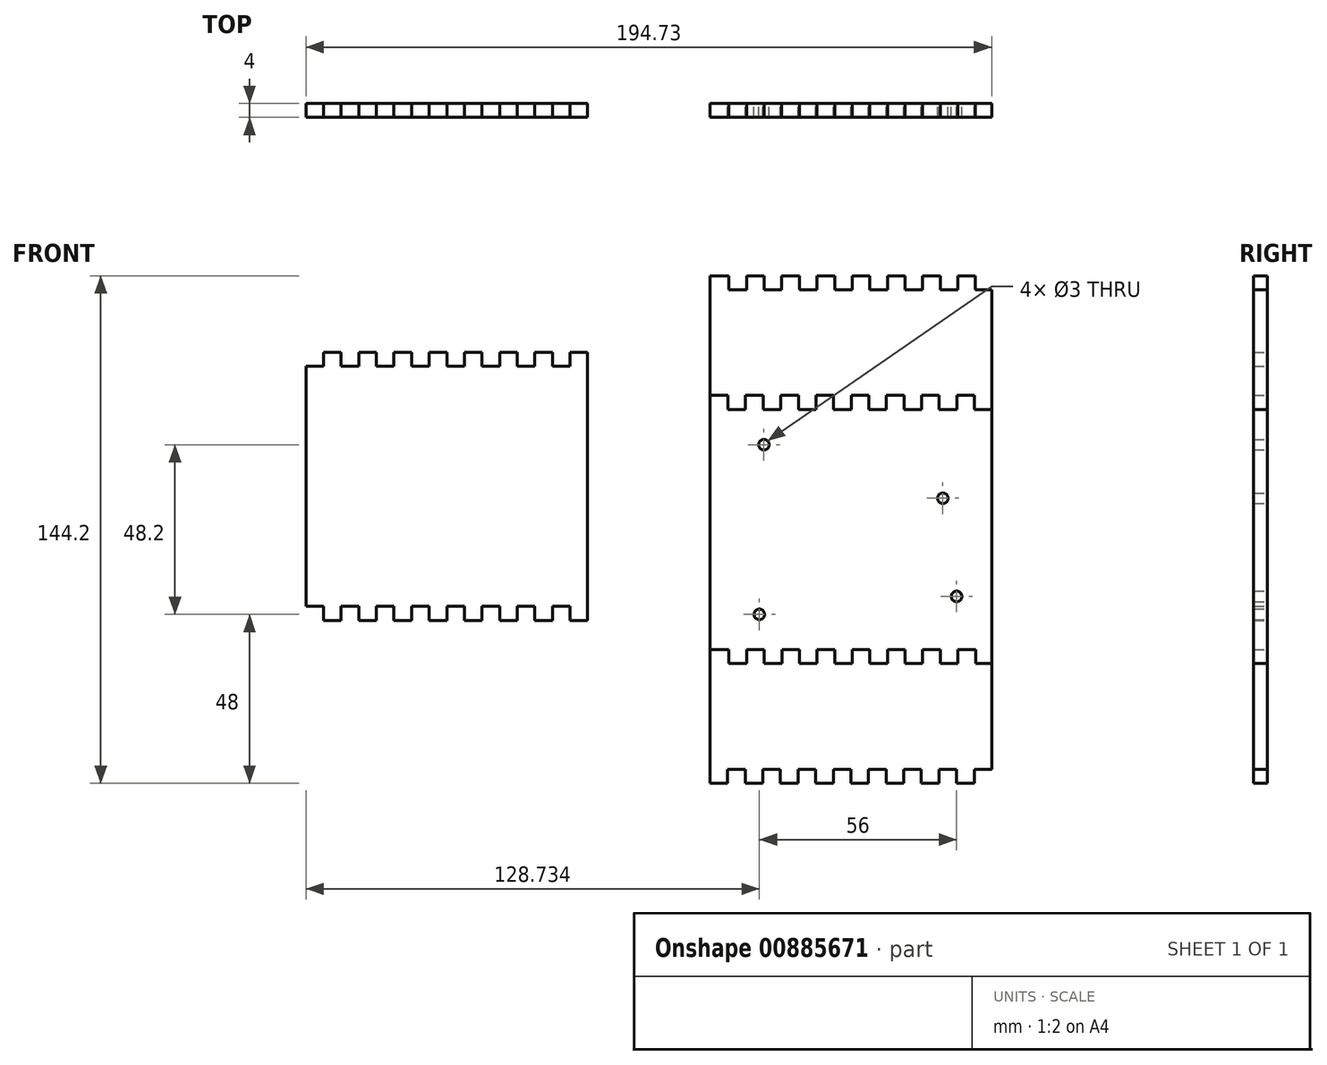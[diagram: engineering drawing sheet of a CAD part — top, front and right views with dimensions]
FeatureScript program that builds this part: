
annotation { "Feature Type Name" : "Feature", "Feature Type Description" : "" }
export const myFeature = defineFeature(function(context is Context, id is Id, definition is map)
    precondition{}
    {
        {
            var Q0;
            Q0=qCreatedBy(makeId("Front.planeOp"),FACE);
            var sketch = newSketch(context, id + "F0", { "sketchPlane" : qUnion([Q0])});
            skLineSegment(sketch, "E0.top", {"start": v(-30.4, -49.1) * mm, "end": v(-25.4, -49.1) * mm});
            skLineSegment(sketch, "E0.left", {"start": v(-35.8, 27.1) * mm, "end": v(-35.8, -45.1) * mm});
            skLineSegment(sketch, "E0.right", {"start": v(44.2, 23.1) * mm, "end": v(44.2, -49.1) * mm});
            skLineSegment(sketch, "E1.1.0.0", {"start": v(-30.7, 23.1) * mm, "end": v(-25.7, 23.1) * mm});
            skLineSegment(sketch, "E1.1.0.1", {"start": v(-30.7, 27.1) * mm, "end": v(-30.7, 23.1) * mm});
            skLineSegment(sketch, "E1.1.0.2", {"start": v(-25.7, 27.1) * mm, "end": v(-25.7, 23.1) * mm});
            skLineSegment(sketch, "E1.2.0.0", {"start": v(-20.7, 23.1) * mm, "end": v(-15.7, 23.1) * mm});
            skLineSegment(sketch, "E1.2.0.1", {"start": v(-20.7, 27.1) * mm, "end": v(-20.7, 23.1) * mm});
            skLineSegment(sketch, "E1.2.0.2", {"start": v(-15.7, 27.1) * mm, "end": v(-15.7, 23.1) * mm});
            skLineSegment(sketch, "E1.3.0.0", {"start": v(-10.7, 23.1) * mm, "end": v(-5.7, 23.1) * mm});
            skLineSegment(sketch, "E1.3.0.1", {"start": v(-10.7, 27.1) * mm, "end": v(-10.7, 23.1) * mm});
            skLineSegment(sketch, "E1.3.0.2", {"start": v(-5.7, 27.1) * mm, "end": v(-5.7, 23.1) * mm});
            skLineSegment(sketch, "E1.4.0.0", {"start": v(-0.7, 23.1) * mm, "end": v(4.3, 23.1) * mm});
            skLineSegment(sketch, "E1.4.0.1", {"start": v(-0.7, 27.1) * mm, "end": v(-0.7, 23.1) * mm});
            skLineSegment(sketch, "E1.4.0.2", {"start": v(4.3, 27.1) * mm, "end": v(4.3, 23.1) * mm});
            skLineSegment(sketch, "E1.5.0.0", {"start": v(9.3, 23.1) * mm, "end": v(14.3, 23.1) * mm});
            skLineSegment(sketch, "E1.5.0.1", {"start": v(9.3, 27.1) * mm, "end": v(9.3, 23.1) * mm});
            skLineSegment(sketch, "E1.5.0.2", {"start": v(14.3, 27.1) * mm, "end": v(14.3, 23.1) * mm});
            skLineSegment(sketch, "E1.6.0.0", {"start": v(19.3, 23.1) * mm, "end": v(24.3, 23.1) * mm});
            skLineSegment(sketch, "E1.6.0.1", {"start": v(19.3, 27.1) * mm, "end": v(19.3, 23.1) * mm});
            skLineSegment(sketch, "E1.6.0.2", {"start": v(24.3, 27.1) * mm, "end": v(24.3, 23.1) * mm});
            skLineSegment(sketch, "E1.7.0.0", {"start": v(29.3, 23.1) * mm, "end": v(34.3, 23.1) * mm});
            skLineSegment(sketch, "E1.7.0.1", {"start": v(29.3, 27.1) * mm, "end": v(29.3, 23.1) * mm});
            skLineSegment(sketch, "E1.7.0.2", {"start": v(34.3, 27.1) * mm, "end": v(34.3, 23.1) * mm});
            skLineSegment(sketch, "E1.8.0.0", {"start": v(39.3, 23.1) * mm, "end": v(44.2, 23.1) * mm});
            skLineSegment(sketch, "E1.8.0.1", {"start": v(39.3, 27.1) * mm, "end": v(39.3, 23.1) * mm});
            skLineSegment(sketch, "E2.trimOffspring", {"start": v(-25.7, 27.1) * mm, "end": v(-20.7, 27.1) * mm});
            skLineSegment(sketch, "E3.trimOffspring", {"start": v(-15.7, 27.1) * mm, "end": v(-10.7, 27.1) * mm});
            skLineSegment(sketch, "E4.trimOffspring", {"start": v(-5.7, 27.1) * mm, "end": v(-0.7, 27.1) * mm});
            skLineSegment(sketch, "E5.trimOffspring", {"start": v(4.3, 27.1) * mm, "end": v(9.3, 27.1) * mm});
            skLineSegment(sketch, "E6.trimOffspring", {"start": v(14.3, 27.1) * mm, "end": v(19.3, 27.1) * mm});
            skLineSegment(sketch, "E7.trimOffspring", {"start": v(24.3, 27.1) * mm, "end": v(29.3, 27.1) * mm});
            skLineSegment(sketch, "E8.trimOffspring", {"start": v(34.3, 27.1) * mm, "end": v(39.3, 27.1) * mm});
            skLineSegment(sketch, "E9", {"start": v(44.2, 23.1) * mm, "end": v(44.2, 57.1) * mm});
            skLineSegment(sketch, "E10", {"start": v(39.57, 61.1) * mm, "end": v(34.57, 61.1) * mm});
            skLineSegment(sketch, "E11", {"start": v(-35.8, 61.1) * mm, "end": v(-35.8, 27.1) * mm});
            skCircle(sketch, "E12", {"center": v(30.3, -2.1) * mm, "radius": 1.5 * mm});
            skCircle(sketch, "E13", {"center": v(34.2, -30) * mm, "radius": 1.5 * mm});
            skCircle(sketch, "E14", {"center": v(-20.5, 13.1) * mm, "radius": 1.5 * mm});
            skCircle(sketch, "E15", {"center": v(-21.8, -35.1) * mm, "radius": 1.5 * mm});
            skLineSegment(sketch, "E16", {"start": v(-30.7, 27.1) * mm, "end": v(-35.8, 27.1) * mm});
            skLineSegment(sketch, "E17.1.0.1", {"start": v(-30.4, -45.1) * mm, "end": v(-30.4, -49.1) * mm});
            skLineSegment(sketch, "E17.1.0.2", {"start": v(-25.4, -45.1) * mm, "end": v(-25.4, -49.1) * mm});
            skLineSegment(sketch, "E17.2.0.0", {"start": v(-20.4, -49.1) * mm, "end": v(-15.4, -49.1) * mm});
            skLineSegment(sketch, "E17.2.0.1", {"start": v(-20.4, -45.1) * mm, "end": v(-20.4, -49.1) * mm});
            skLineSegment(sketch, "E17.2.0.2", {"start": v(-15.4, -45.1) * mm, "end": v(-15.4, -49.1) * mm});
            skLineSegment(sketch, "E17.3.0.0", {"start": v(-10.4, -49.1) * mm, "end": v(-5.4, -49.1) * mm});
            skLineSegment(sketch, "E17.3.0.1", {"start": v(-10.4, -45.1) * mm, "end": v(-10.4, -49.1) * mm});
            skLineSegment(sketch, "E17.3.0.2", {"start": v(-5.4, -45.1) * mm, "end": v(-5.4, -49.1) * mm});
            skLineSegment(sketch, "E17.4.0.0", {"start": v(-0.4, -49.1) * mm, "end": v(4.6, -49.1) * mm});
            skLineSegment(sketch, "E17.4.0.1", {"start": v(-0.4, -45.1) * mm, "end": v(-0.4, -49.1) * mm});
            skLineSegment(sketch, "E17.4.0.2", {"start": v(4.6, -45.1) * mm, "end": v(4.6, -49.1) * mm});
            skLineSegment(sketch, "E17.5.0.0", {"start": v(9.6, -49.1) * mm, "end": v(14.6, -49.1) * mm});
            skLineSegment(sketch, "E17.5.0.1", {"start": v(9.6, -45.1) * mm, "end": v(9.6, -49.1) * mm});
            skLineSegment(sketch, "E17.5.0.2", {"start": v(14.6, -45.1) * mm, "end": v(14.6, -49.1) * mm});
            skLineSegment(sketch, "E17.6.0.0", {"start": v(19.6, -49.1) * mm, "end": v(24.6, -49.1) * mm});
            skLineSegment(sketch, "E17.6.0.1", {"start": v(19.6, -45.1) * mm, "end": v(19.6, -49.1) * mm});
            skLineSegment(sketch, "E17.6.0.2", {"start": v(24.6, -45.1) * mm, "end": v(24.6, -49.1) * mm});
            skLineSegment(sketch, "E17.7.0.0", {"start": v(29.6, -49.1) * mm, "end": v(34.6, -49.1) * mm});
            skLineSegment(sketch, "E17.7.0.1", {"start": v(29.6, -45.1) * mm, "end": v(29.6, -49.1) * mm});
            skLineSegment(sketch, "E17.7.0.2", {"start": v(34.6, -45.1) * mm, "end": v(34.6, -49.1) * mm});
            skLineSegment(sketch, "E17.8.0.1", {"start": v(39.6, -45.1) * mm, "end": v(39.6, -49.1) * mm});
            skLineSegment(sketch, "E18.trimOffspring", {"start": v(-25.4, -45.1) * mm, "end": v(-20.4, -45.1) * mm});
            skLineSegment(sketch, "E19.trimOffspring", {"start": v(-15.4, -45.1) * mm, "end": v(-10.4, -45.1) * mm});
            skLineSegment(sketch, "E20.trimOffspring", {"start": v(-5.4, -45.1) * mm, "end": v(-0.4, -45.1) * mm});
            skLineSegment(sketch, "E21.trimOffspring", {"start": v(4.6, -45.1) * mm, "end": v(9.6, -45.1) * mm});
            skLineSegment(sketch, "E22.trimOffspring", {"start": v(14.6, -45.1) * mm, "end": v(19.6, -45.1) * mm});
            skLineSegment(sketch, "E23.trimOffspring", {"start": v(24.6, -45.1) * mm, "end": v(29.6, -45.1) * mm});
            skLineSegment(sketch, "E24.trimOffspring", {"start": v(34.6, -45.1) * mm, "end": v(39.6, -45.1) * mm});
            skLineSegment(sketch, "E25", {"start": v(-30.4, -45.1) * mm, "end": v(-35.8, -45.1) * mm});
            skLineSegment(sketch, "E26.trimOffspring", {"start": v(39.6, -49.1) * mm, "end": v(44.2, -49.1) * mm});
            skLineSegment(sketch, "E27.top", {"start": v(-30.43, 57.1) * mm, "end": v(-25.43, 57.1) * mm});
            skLineSegment(sketch, "E27.left", {"start": v(-30.43, 61.1) * mm, "end": v(-30.43, 57.1) * mm});
            skLineSegment(sketch, "E27.right", {"start": v(-25.43, 61.1) * mm, "end": v(-25.43, 57.1) * mm});
            skLineSegment(sketch, "E28.trimOffspring", {"start": v(-30.43, 61.1) * mm, "end": v(-35.8, 61.1) * mm});
            skLineSegment(sketch, "E29.1.0.0", {"start": v(-20.43, 61.1) * mm, "end": v(-20.43, 57.1) * mm});
            skLineSegment(sketch, "E29.1.0.1", {"start": v(-20.43, 57.1) * mm, "end": v(-15.43, 57.1) * mm});
            skLineSegment(sketch, "E29.1.0.2", {"start": v(-15.43, 61.1) * mm, "end": v(-15.43, 57.1) * mm});
            skLineSegment(sketch, "E29.2.0.0", {"start": v(-10.43, 61.1) * mm, "end": v(-10.43, 57.1) * mm});
            skLineSegment(sketch, "E29.2.0.1", {"start": v(-10.43, 57.1) * mm, "end": v(-5.43, 57.1) * mm});
            skLineSegment(sketch, "E29.2.0.2", {"start": v(-5.43, 61.1) * mm, "end": v(-5.43, 57.1) * mm});
            skLineSegment(sketch, "E29.3.0.0", {"start": v(-0.43, 61.1) * mm, "end": v(-0.43, 57.1) * mm});
            skLineSegment(sketch, "E29.3.0.1", {"start": v(-0.43, 57.1) * mm, "end": v(4.57, 57.1) * mm});
            skLineSegment(sketch, "E29.3.0.2", {"start": v(4.57, 61.1) * mm, "end": v(4.57, 57.1) * mm});
            skLineSegment(sketch, "E29.4.0.0", {"start": v(9.57, 61.1) * mm, "end": v(9.57, 57.1) * mm});
            skLineSegment(sketch, "E29.4.0.1", {"start": v(9.57, 57.1) * mm, "end": v(14.57, 57.1) * mm});
            skLineSegment(sketch, "E29.4.0.2", {"start": v(14.57, 61.1) * mm, "end": v(14.57, 57.1) * mm});
            skLineSegment(sketch, "E29.5.0.0", {"start": v(19.57, 61.1) * mm, "end": v(19.57, 57.1) * mm});
            skLineSegment(sketch, "E29.5.0.1", {"start": v(19.57, 57.1) * mm, "end": v(24.57, 57.1) * mm});
            skLineSegment(sketch, "E29.5.0.2", {"start": v(24.57, 61.1) * mm, "end": v(24.57, 57.1) * mm});
            skLineSegment(sketch, "E29.6.0.0", {"start": v(29.57, 61.1) * mm, "end": v(29.57, 57.1) * mm});
            skLineSegment(sketch, "E29.6.0.1", {"start": v(29.57, 57.1) * mm, "end": v(34.57, 57.1) * mm});
            skLineSegment(sketch, "E29.6.0.2", {"start": v(34.57, 61.1) * mm, "end": v(34.57, 57.1) * mm});
            skLineSegment(sketch, "E29.7.0.0", {"start": v(39.57, 61.1) * mm, "end": v(39.57, 57.1) * mm});
            skLineSegment(sketch, "E29.direction1", {"start": v(-30.43, 57.1) * mm, "end": v(-20.43, 57.1) * mm, "construction": true});
            skLineSegment(sketch, "E30", {"start": v(39.57, 57.1) * mm, "end": v(44.2, 57.1) * mm});
            skLineSegment(sketch, "E31.trimOffspring", {"start": v(-20.43, 61.1) * mm, "end": v(-25.43, 61.1) * mm});
            skLineSegment(sketch, "E32.trimOffspring", {"start": v(-10.43, 61.1) * mm, "end": v(-15.43, 61.1) * mm});
            skLineSegment(sketch, "E33.trimOffspring", {"start": v(-0.43, 61.1) * mm, "end": v(-5.43, 61.1) * mm});
            skLineSegment(sketch, "E34.trimOffspring", {"start": v(9.57, 61.1) * mm, "end": v(4.57, 61.1) * mm});
            skLineSegment(sketch, "E35.trimOffspring", {"start": v(19.57, 61.1) * mm, "end": v(14.57, 61.1) * mm});
            skLineSegment(sketch, "E36.trimOffspring", {"start": v(29.57, 61.1) * mm, "end": v(24.57, 61.1) * mm});
            skLineSegment(sketch, "E37.top", {"start": v(-30.8, -79.1) * mm, "end": v(-25.8, -79.1) * mm});
            skLineSegment(sketch, "E37.left", {"start": v(-30.8, -83.1) * mm, "end": v(-30.8, -79.1) * mm});
            skLineSegment(sketch, "E37.right", {"start": v(-25.8, -83.1) * mm, "end": v(-25.8, -79.1) * mm});
            skLineSegment(sketch, "E38.1.0.0", {"start": v(-20.8, -83.1) * mm, "end": v(-20.8, -79.1) * mm});
            skLineSegment(sketch, "E38.1.0.1", {"start": v(-20.8, -79.1) * mm, "end": v(-15.8, -79.1) * mm});
            skLineSegment(sketch, "E38.1.0.2", {"start": v(-15.8, -83.1) * mm, "end": v(-15.8, -79.1) * mm});
            skLineSegment(sketch, "E38.2.0.0", {"start": v(-10.8, -83.1) * mm, "end": v(-10.8, -79.1) * mm});
            skLineSegment(sketch, "E38.2.0.1", {"start": v(-10.8, -79.1) * mm, "end": v(-5.8, -79.1) * mm});
            skLineSegment(sketch, "E38.2.0.2", {"start": v(-5.8, -83.1) * mm, "end": v(-5.8, -79.1) * mm});
            skLineSegment(sketch, "E38.3.0.0", {"start": v(-0.8, -83.1) * mm, "end": v(-0.8, -79.1) * mm});
            skLineSegment(sketch, "E38.3.0.1", {"start": v(-0.8, -79.1) * mm, "end": v(4.2, -79.1) * mm});
            skLineSegment(sketch, "E38.3.0.2", {"start": v(4.2, -83.1) * mm, "end": v(4.2, -79.1) * mm});
            skLineSegment(sketch, "E38.4.0.0", {"start": v(9.2, -83.1) * mm, "end": v(9.2, -79.1) * mm});
            skLineSegment(sketch, "E38.4.0.1", {"start": v(9.2, -79.1) * mm, "end": v(14.2, -79.1) * mm});
            skLineSegment(sketch, "E38.4.0.2", {"start": v(14.2, -83.1) * mm, "end": v(14.2, -79.1) * mm});
            skLineSegment(sketch, "E38.5.0.0", {"start": v(19.2, -83.1) * mm, "end": v(19.2, -79.1) * mm});
            skLineSegment(sketch, "E38.5.0.1", {"start": v(19.2, -79.1) * mm, "end": v(24.2, -79.1) * mm});
            skLineSegment(sketch, "E38.5.0.2", {"start": v(24.2, -83.1) * mm, "end": v(24.2, -79.1) * mm});
            skLineSegment(sketch, "E38.6.0.0", {"start": v(29.2, -83.1) * mm, "end": v(29.2, -79.1) * mm});
            skLineSegment(sketch, "E38.6.0.1", {"start": v(29.2, -79.1) * mm, "end": v(34.2, -79.1) * mm});
            skLineSegment(sketch, "E38.6.0.2", {"start": v(34.2, -83.1) * mm, "end": v(34.2, -79.1) * mm});
            skLineSegment(sketch, "E38.7.0.0", {"start": v(39.2, -83.1) * mm, "end": v(39.2, -79.1) * mm});
            skLineSegment(sketch, "E38.direction1", {"start": v(-25.8, -83.1) * mm, "end": v(-20.8, -83.1) * mm, "construction": true});
            skLineSegment(sketch, "E39.trimOffspring", {"start": v(-20.8, -83.1) * mm, "end": v(-25.8, -83.1) * mm});
            skLineSegment(sketch, "E40.trimOffspring", {"start": v(-10.8, -83.1) * mm, "end": v(-15.8, -83.1) * mm});
            skLineSegment(sketch, "E41.trimOffspring", {"start": v(-0.8, -83.1) * mm, "end": v(-5.8, -83.1) * mm});
            skLineSegment(sketch, "E42.trimOffspring", {"start": v(9.2, -83.1) * mm, "end": v(4.2, -83.1) * mm});
            skLineSegment(sketch, "E43.trimOffspring", {"start": v(19.2, -83.1) * mm, "end": v(14.2, -83.1) * mm});
            skLineSegment(sketch, "E44.trimOffspring", {"start": v(29.2, -83.1) * mm, "end": v(24.2, -83.1) * mm});
            skLineSegment(sketch, "E45.trimOffspring", {"start": v(-30.8, -83.1) * mm, "end": v(-35.8, -83.1) * mm});
            skLineSegment(sketch, "E46", {"start": v(34.2, -83.1) * mm, "end": v(39.2, -83.1) * mm});
            skLineSegment(sketch, "E47", {"start": v(39.2, -79.1) * mm, "end": v(44.2, -79.1) * mm});
            skLineSegment(sketch, "E48", {"start": v(44.2, -79.1) * mm, "end": v(44.2, -49.1) * mm});
            skLineSegment(sketch, "E49", {"start": v(-35.8, -45.1) * mm, "end": v(-35.8, -83.1) * mm});
            skLineSegment(sketch, "E50.MirrorCS", {"start": v(-145.54, 39.34) * mm, "end": v(-140.54, 39.34) * mm});
            skLineSegment(sketch, "E51.MirrorCS", {"start": v(-140.54, 35.34) * mm, "end": v(-140.54, 39.34) * mm});
            skLineSegment(sketch, "E52.MirrorCS", {"start": v(-115.54, 35.34) * mm, "end": v(-120.54, 35.34) * mm});
            skLineSegment(sketch, "E53.MirrorCS", {"start": v(-135.54, 35.34) * mm, "end": v(-140.54, 35.34) * mm});
            skLineSegment(sketch, "E54.MirrorCS", {"start": v(-85.54, 35.34) * mm, "end": v(-90.54, 35.34) * mm});
            skLineSegment(sketch, "E55.MirrorCS", {"start": v(-135.54, 35.34) * mm, "end": v(-135.54, 39.34) * mm});
            skLineSegment(sketch, "E56.MirrorCS", {"start": v(-135.54, 39.34) * mm, "end": v(-130.54, 39.34) * mm});
            skLineSegment(sketch, "E57.MirrorCS", {"start": v(-80.54, 35.34) * mm, "end": v(-80.54, 39.34) * mm});
            skLineSegment(sketch, "E58.MirrorCS", {"start": v(-75.54, 35.34) * mm, "end": v(-80.54, 35.34) * mm});
            skLineSegment(sketch, "E59.MirrorCS", {"start": v(-120.54, 35.34) * mm, "end": v(-120.54, 39.34) * mm});
            skLineSegment(sketch, "E60.MirrorCS", {"start": v(-90.54, 35.34) * mm, "end": v(-90.54, 39.34) * mm});
            skLineSegment(sketch, "E61.MirrorCS", {"start": v(-85.54, 35.34) * mm, "end": v(-85.54, 39.34) * mm});
            skLineSegment(sketch, "E62.MirrorCS", {"start": v(-100.54, 35.34) * mm, "end": v(-100.54, 39.34) * mm});
            skLineSegment(sketch, "E63.MirrorCS", {"start": v(-105.54, 35.34) * mm, "end": v(-105.54, 39.34) * mm});
            skLineSegment(sketch, "E64.MirrorCS", {"start": v(-95.54, 35.34) * mm, "end": v(-95.54, 39.34) * mm});
            skLineSegment(sketch, "E65.MirrorCS", {"start": v(-105.54, 35.34) * mm, "end": v(-110.54, 35.34) * mm});
            skLineSegment(sketch, "E66.MirrorCS", {"start": v(-145.54, 35.34) * mm, "end": v(-145.54, 39.34) * mm});
            skLineSegment(sketch, "E67.MirrorCS", {"start": v(-95.54, 35.34) * mm, "end": v(-100.54, 35.34) * mm});
            skLineSegment(sketch, "E68.MirrorCS", {"start": v(-85.54, 39.34) * mm, "end": v(-80.54, 39.34) * mm});
            skLineSegment(sketch, "E69.MirrorCS", {"start": v(-110.54, 35.34) * mm, "end": v(-110.54, 39.34) * mm});
            skLineSegment(sketch, "E70.MirrorCS", {"start": v(-75.54, 35.34) * mm, "end": v(-75.54, 39.34) * mm});
            skLineSegment(sketch, "E71.MirrorCS", {"start": v(-125.54, 35.34) * mm, "end": v(-130.54, 35.34) * mm});
            skLineSegment(sketch, "E72.MirrorCS", {"start": v(-145.54, 35.34) * mm, "end": v(-150.54, 35.34) * mm});
            skLineSegment(sketch, "E73.MirrorCS", {"start": v(-125.54, 35.34) * mm, "end": v(-125.54, 39.34) * mm});
            skLineSegment(sketch, "E74.MirrorCS", {"start": v(-115.54, 35.34) * mm, "end": v(-115.54, 39.34) * mm});
            skLineSegment(sketch, "E75.MirrorCS", {"start": v(-95.54, 39.34) * mm, "end": v(-90.54, 39.34) * mm});
            skLineSegment(sketch, "E76.MirrorCS", {"start": v(-115.54, 39.34) * mm, "end": v(-110.54, 39.34) * mm});
            skLineSegment(sketch, "E77.MirrorCS", {"start": v(-105.54, 39.34) * mm, "end": v(-100.54, 39.34) * mm});
            skLineSegment(sketch, "E78.MirrorCS", {"start": v(-125.54, 39.34) * mm, "end": v(-120.54, 39.34) * mm});
            skLineSegment(sketch, "E79.MirrorCS", {"start": v(-130.54, 35.34) * mm, "end": v(-130.54, 39.34) * mm});
            skLineSegment(sketch, "E80.MirrorCS", {"start": v(-75.54, 39.34) * mm, "end": v(-70.54, 39.34) * mm});
            skLineSegment(sketch, "E81.MirrorCS", {"start": v(-150.54, -32.86) * mm, "end": v(-150.54, 35.34) * mm});
            skLineSegment(sketch, "E82.MirrorCS", {"start": v(-70.54, 39.34) * mm, "end": v(-70.54, -36.86) * mm});
            skLineSegment(sketch, "E83.MirrorCS", {"start": v(-80.54, -32.86) * mm, "end": v(-80.54, -36.86) * mm});
            skLineSegment(sketch, "E84.MirrorCS", {"start": v(-105.54, -32.86) * mm, "end": v(-105.54, -36.86) * mm});
            skLineSegment(sketch, "E85.MirrorCS", {"start": v(-85.54, -32.86) * mm, "end": v(-85.54, -36.86) * mm});
            skLineSegment(sketch, "E86.MirrorCS", {"start": v(-95.54, -32.86) * mm, "end": v(-95.54, -36.86) * mm});
            skLineSegment(sketch, "E87.MirrorCS", {"start": v(-145.54, -32.86) * mm, "end": v(-145.54, -36.86) * mm});
            skLineSegment(sketch, "E88.MirrorCS", {"start": v(-125.54, -32.86) * mm, "end": v(-125.54, -36.86) * mm});
            skLineSegment(sketch, "E89.MirrorCS", {"start": v(-100.54, -32.86) * mm, "end": v(-100.54, -36.86) * mm});
            skLineSegment(sketch, "E90.MirrorCS", {"start": v(-115.54, -32.86) * mm, "end": v(-115.54, -36.86) * mm});
            skLineSegment(sketch, "E91.MirrorCS", {"start": v(-135.54, -32.86) * mm, "end": v(-140.54, -32.86) * mm});
            skLineSegment(sketch, "E92.MirrorCS", {"start": v(-140.54, -32.86) * mm, "end": v(-140.54, -36.86) * mm});
            skLineSegment(sketch, "E93.MirrorCS", {"start": v(-75.54, -36.86) * mm, "end": v(-70.54, -36.86) * mm});
            skLineSegment(sketch, "E94.MirrorCS", {"start": v(-90.54, -32.86) * mm, "end": v(-90.54, -36.86) * mm});
            skLineSegment(sketch, "E95.MirrorCS", {"start": v(-115.54, -32.86) * mm, "end": v(-120.54, -32.86) * mm});
            skLineSegment(sketch, "E96.MirrorCS", {"start": v(-95.54, -36.86) * mm, "end": v(-90.54, -36.86) * mm});
            skLineSegment(sketch, "E97.MirrorCS", {"start": v(-120.54, -32.86) * mm, "end": v(-120.54, -36.86) * mm});
            skLineSegment(sketch, "E98.MirrorCS", {"start": v(-75.54, -32.86) * mm, "end": v(-75.54, -36.86) * mm});
            skLineSegment(sketch, "E99.MirrorCS", {"start": v(-130.54, -32.86) * mm, "end": v(-130.54, -36.86) * mm});
            skLineSegment(sketch, "E100.MirrorCS", {"start": v(-135.54, -32.86) * mm, "end": v(-135.54, -36.86) * mm});
            skLineSegment(sketch, "E101.MirrorCS", {"start": v(-110.54, -32.86) * mm, "end": v(-110.54, -36.86) * mm});
            skLineSegment(sketch, "E102.MirrorCS", {"start": v(-145.54, -32.86) * mm, "end": v(-150.54, -32.86) * mm});
            skLineSegment(sketch, "E103.MirrorCS", {"start": v(-145.54, -36.86) * mm, "end": v(-140.54, -36.86) * mm});
            skLineSegment(sketch, "E104.MirrorCS", {"start": v(-75.54, -32.86) * mm, "end": v(-80.54, -32.86) * mm});
            skLineSegment(sketch, "E105.MirrorCS", {"start": v(-85.54, -32.86) * mm, "end": v(-90.54, -32.86) * mm});
            skLineSegment(sketch, "E106.MirrorCS", {"start": v(-105.54, -32.86) * mm, "end": v(-110.54, -32.86) * mm});
            skLineSegment(sketch, "E107.MirrorCS", {"start": v(-95.54, -32.86) * mm, "end": v(-100.54, -32.86) * mm});
            skLineSegment(sketch, "E108.MirrorCS", {"start": v(-125.54, -32.86) * mm, "end": v(-130.54, -32.86) * mm});
            skLineSegment(sketch, "E109.MirrorCS", {"start": v(-105.54, -36.86) * mm, "end": v(-100.54, -36.86) * mm});
            skLineSegment(sketch, "E110.MirrorCS", {"start": v(-135.54, -36.86) * mm, "end": v(-130.54, -36.86) * mm});
            skLineSegment(sketch, "E111.MirrorCS", {"start": v(-115.54, -36.86) * mm, "end": v(-110.54, -36.86) * mm});
            skLineSegment(sketch, "E112.MirrorCS", {"start": v(-85.54, -36.86) * mm, "end": v(-80.54, -36.86) * mm});
            skLineSegment(sketch, "E113.MirrorCS", {"start": v(-125.54, -36.86) * mm, "end": v(-120.54, -36.86) * mm});
            skSolve(sketch);
        }
        {
            var Q0;
            Q0=makeQuery(id+"F0.imprint","IMPRINT",FACE,{"disambiguationData":[TD([[makeQuery(id+"F0.imprint","IMPRINT",EDGE,{"derivedFrom":sQuery(id+"F0.wireOp",EDGE,"E1.1.0.0")}),1.0]])]});
            extrude(context, id + "F1", {"entities" : qUnion([Q0]), "depth" : 4 * mm, "offsetDistance" : 25 * mm});
        }
        {
            var Q0;
            Q0=makeQuery(id+"F0.imprint","IMPRINT",FACE,{"disambiguationData":[TD([[makeQuery(id+"F0.imprint","IMPRINT",EDGE,{"derivedFrom":sQuery(id+"F0.wireOp",EDGE,"E0.top")}),-1.0]])]});
            extrude(context, id + "F2", {"entities" : qUnion([Q0]), "depth" : 4 * mm, "offsetDistance" : 25 * mm});
        }
        {
            var Q0;
            Q0=makeQuery(id+"F0.imprint","IMPRINT",FACE,{"disambiguationData":[TD([[makeQuery(id+"F0.imprint","IMPRINT",EDGE,{"derivedFrom":sQuery(id+"F0.wireOp",EDGE,"E0.left")}),1.0]])]});
            extrude(context, id + "F3", {"entities" : qUnion([Q0]), "depth" : 4 * mm, "offsetDistance" : 25 * mm});
        }
        {
            var Q0;
            Q0=makeQuery(id+"F0.imprint","IMPRINT",FACE,{"disambiguationData":[TD([[makeQuery(id+"F0.imprint","IMPRINT",EDGE,{"derivedFrom":sQuery(id+"F0.wireOp",EDGE,"E50.MirrorCS")}),-1.0]])]});
            extrude(context, id + "F4", {"entities" : qUnion([Q0]), "depth" : 4 * mm, "offsetDistance" : 25 * mm});
        }
    });
